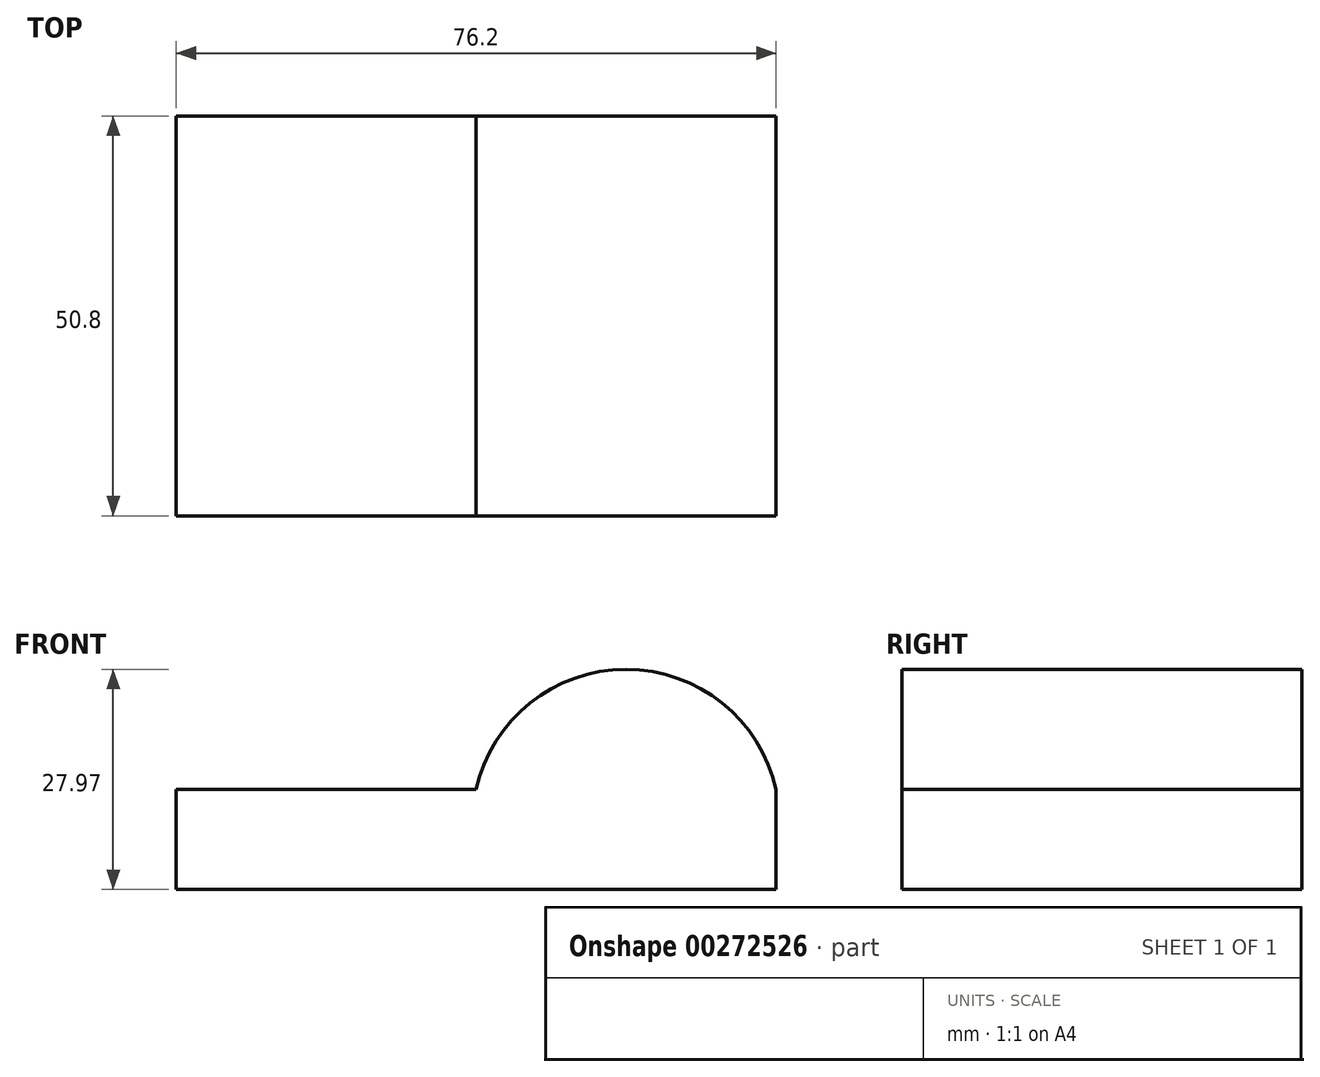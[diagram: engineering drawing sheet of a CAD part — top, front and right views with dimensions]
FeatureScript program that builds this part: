
annotation { "Feature Type Name" : "Feature", "Feature Type Description" : "" }
export const myFeature = defineFeature(function(context is Context, id is Id, definition is map)
    precondition{}
    {
        {
            var Q0;
            Q0=qCreatedBy(makeId("Front.planeOp"),FACE);
            var sketch = newSketch(context, id + "F0", { "sketchPlane" : qUnion([Q0])});
            skLineSegment(sketch, "E0.bottom", {"start": v(0, 0) * mm, "end": v(-76.2, 0) * mm});
            skLineSegment(sketch, "E0.left", {"start": v(0, 0) * mm, "end": v(0, 12.7) * mm});
            skLineSegment(sketch, "E0.right", {"start": v(-76.2, 0) * mm, "end": v(-76.2, 12.7) * mm});
            skLineSegment(sketch, "E1", {"start": v(-76.2, 12.7) * mm, "end": v(-38.1, 12.7) * mm});
            skArc(sketch, "E2", {"start": v(0, 12.7) * mm, "mid": v(-19.05, 27.97) * mm, "end": v(-38.1, 12.7) * mm});
            skSolve(sketch);
        }
        {
            var Q0;
            Q0 = qSketchRegion(id + "F0", true);
            extrude(context, id + "F1", {"entities" : qUnion([Q0]), "depth" : 50.8 * mm});
        }
    });
